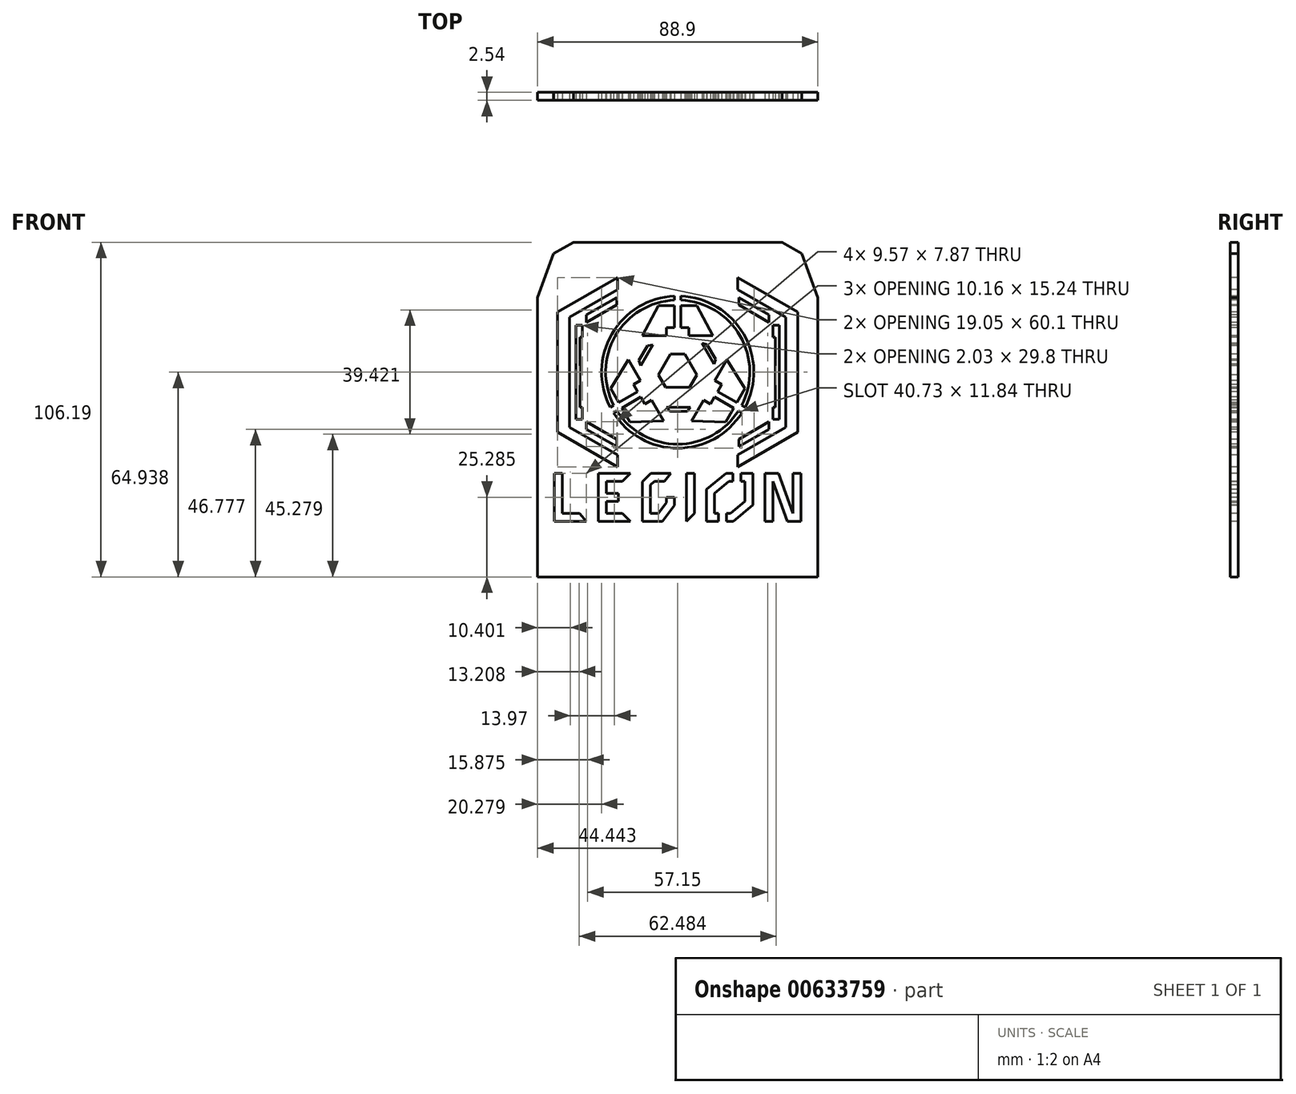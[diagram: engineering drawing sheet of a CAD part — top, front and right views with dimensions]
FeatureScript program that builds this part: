
annotation { "Feature Type Name" : "Feature", "Feature Type Description" : "" }
export const myFeature = defineFeature(function(context is Context, id is Id, definition is map)
    precondition{}
    {
        {
            var Q0;
            Q0=qCreatedBy(makeId("Front.planeOp"),FACE);
            var sketch = newSketch(context, id + "F0", { "sketchPlane" : qUnion([Q0])});
            skLineSegment(sketch, "E0.0", {"start": v(-38.1, -19.1) * mm, "end": v(-38.1, 19) * mm});
            skLineSegment(sketch, "E0.1", {"start": v(-38.1, 19) * mm, "end": v(-19.05, 30) * mm});
            skLineSegment(sketch, "E0.2", {"start": v(19.05, 30) * mm, "end": v(38.1, 19) * mm});
            skLineSegment(sketch, "E0.3", {"start": v(38.1, 19) * mm, "end": v(38.1, -19.1) * mm});
            skLineSegment(sketch, "E0.4", {"start": v(38.1, -19.1) * mm, "end": v(19.05, -30.1) * mm});
            skLineSegment(sketch, "E0.5", {"start": v(-19.05, -30.1) * mm, "end": v(-38.1, -19.1) * mm});
            skLineSegment(sketch, "E1", {"start": v(-19.05, -30.1) * mm, "end": v(-19.05, -26.3) * mm});
            skLineSegment(sketch, "E2", {"start": v(19.05, 30) * mm, "end": v(19.05, 26.19) * mm});
            skPoint(sketch, "E3.orphan", {"position": v(0, 41) * mm});
            skPoint(sketch, "E4.orphan", {"position": v(0, -41.1) * mm});
            skLineSegment(sketch, "E5", {"start": v(19.05, -26.3) * mm, "end": v(34.29, -17.5) * mm});
            skLineSegment(sketch, "E6", {"start": v(34.29, -17.5) * mm, "end": v(34.29, 17.39) * mm});
            skLineSegment(sketch, "E7", {"start": v(34.29, 17.39) * mm, "end": v(19.05, 26.19) * mm});
            skLineSegment(sketch, "E8.trimOffspring", {"start": v(19.05, -26.3) * mm, "end": v(19.05, -30.1) * mm});
            skLineSegment(sketch, "E9", {"start": v(-19.05, 26.19) * mm, "end": v(-34.3, 17.39) * mm});
            skLineSegment(sketch, "E10", {"start": v(-34.29, 17.39) * mm, "end": v(-34.29, -17.5) * mm});
            skLineSegment(sketch, "E11", {"start": v(-34.29, -17.5) * mm, "end": v(-19.05, -26.3) * mm});
            skLineSegment(sketch, "E12.trimOffspring", {"start": v(-19.05, 26.19) * mm, "end": v(-19.05, 30) * mm});
            skSolve(sketch);
        }
        {
            var Q0;
            Q0=makeQuery(id+"F0.imprint","IMPRINT",FACE,{"disambiguationData":[TD([[makeQuery(id+"F0.imprint","IMPRINT",EDGE,{"derivedFrom":sQuery(id+"F0.wireOp",EDGE,"E0.0")}),-1.0]])]});
            var sketch = newSketch(context, id + "F1", { "sketchPlane" : qUnion([Q0])});
            skLineSegment(sketch, "E13", {"start": v(-1.02, 14.1) * mm, "end": v(-3.56, 14.1) * mm});
            skLineSegment(sketch, "E14", {"start": v(-3.56, 14.1) * mm, "end": v(-3.56, 11.56) * mm});
            skLineSegment(sketch, "E15", {"start": v(-3.56, 11.56) * mm, "end": v(-11.18, 11.56) * mm});
            skLineSegment(sketch, "E16", {"start": v(1.02, 14.1) * mm, "end": v(3.56, 14.1) * mm});
            skLineSegment(sketch, "E17", {"start": v(3.56, 14.1) * mm, "end": v(3.56, 11.56) * mm});
            skLineSegment(sketch, "E18", {"start": v(3.56, 11.56) * mm, "end": v(11.18, 11.56) * mm});
            skLineSegment(sketch, "E19", {"start": v(-11.18, 11.56) * mm, "end": v(-6.1, 21.08) * mm});
            skLineSegment(sketch, "E20", {"start": v(11.18, 11.56) * mm, "end": v(6.1, 21.08) * mm});
            skLineSegment(sketch, "E21", {"start": v(-6.1, 21.08) * mm, "end": v(-1.02, 21.08) * mm});
            skLineSegment(sketch, "E22", {"start": v(-1.02, 14.1) * mm, "end": v(-1.02, 21.08) * mm});
            skLineSegment(sketch, "E23", {"start": v(1.02, 14.1) * mm, "end": v(1.02, 21.08) * mm});
            skLineSegment(sketch, "E24.trimOffspring", {"start": v(1.02, 21.08) * mm, "end": v(6.1, 21.08) * mm});
            skLineSegment(sketch, "E25.1.0", {"start": v(-8.23, -8.86) * mm, "end": v(-4.42, -15.46) * mm});
            skLineSegment(sketch, "E25.1.1", {"start": v(-4.42, -15.46) * mm, "end": v(-15.2, -15.82) * mm});
            skLineSegment(sketch, "E25.1.2", {"start": v(-15.2, -15.82) * mm, "end": v(-17.75, -11.42) * mm});
            skLineSegment(sketch, "E25.1.3", {"start": v(-11.7, -7.93) * mm, "end": v(-17.75, -11.42) * mm});
            skLineSegment(sketch, "E25.1.4", {"start": v(-11.7, -7.93) * mm, "end": v(-10.43, -10.13) * mm});
            skLineSegment(sketch, "E25.1.5", {"start": v(-10.43, -10.13) * mm, "end": v(-8.23, -8.86) * mm});
            skLineSegment(sketch, "E25.1.6", {"start": v(-13.98, -3.97) * mm, "end": v(-11.79, -2.7) * mm});
            skLineSegment(sketch, "E25.1.7", {"start": v(-12.71, -6.17) * mm, "end": v(-13.98, -3.97) * mm});
            skLineSegment(sketch, "E25.1.8", {"start": v(-11.79, -2.7) * mm, "end": v(-15.6, 3.9) * mm});
            skLineSegment(sketch, "E25.1.9", {"start": v(-15.6, 3.9) * mm, "end": v(-21.3, -5.26) * mm});
            skLineSegment(sketch, "E25.1.10", {"start": v(-12.71, -6.17) * mm, "end": v(-18.76, -9.66) * mm});
            skLineSegment(sketch, "E25.1.11", {"start": v(-18.76, -9.66) * mm, "end": v(-21.3, -5.26) * mm});
            skLineSegment(sketch, "E25.2.0", {"start": v(11.79, -2.7) * mm, "end": v(15.6, 3.9) * mm});
            skLineSegment(sketch, "E25.2.1", {"start": v(15.6, 3.9) * mm, "end": v(21.3, -5.26) * mm});
            skLineSegment(sketch, "E25.2.2", {"start": v(21.3, -5.26) * mm, "end": v(18.76, -9.66) * mm});
            skLineSegment(sketch, "E25.2.3", {"start": v(12.71, -6.17) * mm, "end": v(18.76, -9.66) * mm});
            skLineSegment(sketch, "E25.2.4", {"start": v(12.71, -6.17) * mm, "end": v(13.98, -3.97) * mm});
            skLineSegment(sketch, "E25.2.5", {"start": v(13.98, -3.97) * mm, "end": v(11.79, -2.7) * mm});
            skLineSegment(sketch, "E25.2.6", {"start": v(10.43, -10.13) * mm, "end": v(8.23, -8.86) * mm});
            skLineSegment(sketch, "E25.2.7", {"start": v(11.7, -7.93) * mm, "end": v(10.43, -10.13) * mm});
            skLineSegment(sketch, "E25.2.8", {"start": v(8.23, -8.86) * mm, "end": v(4.42, -15.46) * mm});
            skLineSegment(sketch, "E25.2.9", {"start": v(4.42, -15.46) * mm, "end": v(15.2, -15.82) * mm});
            skLineSegment(sketch, "E25.2.10", {"start": v(11.7, -7.93) * mm, "end": v(17.75, -11.42) * mm});
            skLineSegment(sketch, "E25.2.11", {"start": v(17.75, -11.42) * mm, "end": v(15.2, -15.82) * mm});
            skPoint(sketch, "E25.center", {"position": v(0, 0) * mm});
            skLineSegment(sketch, "E26", {"start": v(-6.1, -0.88) * mm, "end": v(-2.29, 5.72) * mm});
            skLineSegment(sketch, "E27", {"start": v(-2.29, 5.72) * mm, "end": v(2.29, 5.72) * mm});
            skLineSegment(sketch, "E28", {"start": v(2.29, 5.72) * mm, "end": v(6.1, -0.88) * mm});
            skLineSegment(sketch, "E29", {"start": v(6.1, -0.88) * mm, "end": v(3.8, -4.84) * mm});
            skLineSegment(sketch, "E30", {"start": v(3.8, -4.84) * mm, "end": v(-3.81, -4.84) * mm});
            skLineSegment(sketch, "E31", {"start": v(-3.81, -4.84) * mm, "end": v(-6.1, -0.88) * mm});
            skLineSegment(sketch, "E32", {"start": v(-7.91, 8.67) * mm, "end": v(-11.72, 2.08) * mm});
            skLineSegment(sketch, "E33", {"start": v(-11.72, 2.08) * mm, "end": v(-12.29, 3.63) * mm});
            skLineSegment(sketch, "E34", {"start": v(-12.29, 3.63) * mm, "end": v(-9.54, 8.39) * mm});
            skLineSegment(sketch, "E35", {"start": v(-9.54, 8.39) * mm, "end": v(-7.91, 8.67) * mm});
            skLineSegment(sketch, "E36", {"start": v(-11.72, 2.08) * mm, "end": v(-12.86, 2.73) * mm});
            skLineSegment(sketch, "E37", {"start": v(-7.91, 8.67) * mm, "end": v(-9.11, 9.37) * mm});
            skLineSegment(sketch, "E38.1.0", {"start": v(-2.5, -12.46) * mm, "end": v(-3.56, -11.19) * mm});
            skLineSegment(sketch, "E38.1.1", {"start": v(3, -12.46) * mm, "end": v(-2.5, -12.46) * mm});
            skLineSegment(sketch, "E38.1.2", {"start": v(-3.56, -11.19) * mm, "end": v(4.06, -11.19) * mm});
            skLineSegment(sketch, "E38.1.3", {"start": v(4.06, -11.19) * mm, "end": v(3, -12.46) * mm});
            skLineSegment(sketch, "E38.2.0", {"start": v(12.04, 4.07) * mm, "end": v(11.47, 2.52) * mm});
            skLineSegment(sketch, "E38.2.1", {"start": v(9.3, 8.83) * mm, "end": v(12.04, 4.07) * mm});
            skLineSegment(sketch, "E38.2.2", {"start": v(11.47, 2.52) * mm, "end": v(7.66, 9.11) * mm});
            skLineSegment(sketch, "E38.2.3", {"start": v(7.66, 9.11) * mm, "end": v(9.3, 8.83) * mm});
            skArc(sketch, "E39", {"start": v(-1.01, 24.1) * mm, "mid": v(-20.9, 12.08) * mm, "end": v(-21.4, -11.16) * mm});
            skLineSegment(sketch, "E40", {"start": v(-1.01, 22.84) * mm, "end": v(-1.01, 24.1) * mm});
            skLineSegment(sketch, "E41", {"start": v(1.04, 22.84) * mm, "end": v(1.04, 24.1) * mm});
            skLineSegment(sketch, "E42.1.0", {"start": v(-19.27, -12.3) * mm, "end": v(-20.37, -12.93) * mm});
            skLineSegment(sketch, "E42.1.1", {"start": v(-20.3, -10.52) * mm, "end": v(-21.4, -11.16) * mm});
            skLineSegment(sketch, "E42.2.0", {"start": v(20.28, -10.54) * mm, "end": v(21.38, -11.18) * mm});
            skLineSegment(sketch, "E42.2.1", {"start": v(19.26, -12.32) * mm, "end": v(20.36, -12.95) * mm});
            skArc(sketch, "E43.trimOffspring", {"start": v(-20.37, -12.93) * mm, "mid": v(-0.01, -24.13) * mm, "end": v(20.36, -12.95) * mm});
            skArc(sketch, "E44.trimOffspring", {"start": v(21.38, -11.18) * mm, "mid": v(20.9, 12.05) * mm, "end": v(1.04, 24.1) * mm});
            skArc(sketch, "E45", {"start": v(20.28, -10.54) * mm, "mid": v(19.8, 11.42) * mm, "end": v(1.04, 22.84) * mm});
            skArc(sketch, "E46.trimOffspring", {"start": v(-19.27, -12.3) * mm, "mid": v(-0.01, -22.86) * mm, "end": v(19.26, -12.32) * mm});
            skArc(sketch, "E47.trimOffspring", {"start": v(-1.01, 22.84) * mm, "mid": v(-19.8, 11.44) * mm, "end": v(-20.3, -10.52) * mm});
            skSolve(sketch);
        }
        {
            var Q0;
            Q0=makeQuery(id+"F0.imprint","IMPRINT",FACE,{"disambiguationData":[TD([[makeQuery(id+"F0.imprint","IMPRINT",EDGE,{"derivedFrom":sQuery(id+"F0.wireOp",EDGE,"E0.0")}),-1.0]])]});
            var sketch = newSketch(context, id + "F2", { "sketchPlane" : qUnion([Q0])});
            skLineSegment(sketch, "E48.bottom", {"start": v(-44.45, -65) * mm, "end": v(44.45, -65) * mm});
            skLineSegment(sketch, "E48.top", {"start": v(-44.45, 49.3) * mm, "end": v(44.45, 49.3) * mm});
            skLineSegment(sketch, "E48.left", {"start": v(-44.45, -65) * mm, "end": v(-44.45, 49.3) * mm});
            skLineSegment(sketch, "E48.right", {"start": v(44.45, -65) * mm, "end": v(44.45, 49.3) * mm});
            skSolve(sketch);
        }
        {
            var Q0;
            Q0=makeQuery(id+"F2.imprint","IMPRINT",FACE,{"disambiguationData":[TD([[makeQuery(id+"F2.imprint","IMPRINT",EDGE,{"derivedFrom":sQuery(id+"F2.wireOp",EDGE,"E48.bottom")}),1.0]])]});
            extrude(context, id + "F3", {"entities" : qUnion([Q0]), "oppositeDirection" : true, "depth" : 2.54 * mm, "offsetDistance" : 25.4 * mm});
        }
        {
            var Q0;
            Q0=makeQuery(id+"F0.imprint","IMPRINT",FACE,{"disambiguationData":[TD([[makeQuery(id+"F0.imprint","IMPRINT",EDGE,{"derivedFrom":sQuery(id+"F0.wireOp",EDGE,"E0.2")}),-1.0]])]});
            extrude(context, id + "F4", {"entities" : qUnion([Q0]), "operationType" : NewBodyOperationType.REMOVE, "oppositeDirection" : true, "depth" : 25.4 * mm, "offsetDistance" : 25.4 * mm});
        }
        {
            var Q0;
            Q0=makeQuery(id+"F1.imprint","IMPRINT",FACE,{"disambiguationData":[TD([[makeQuery(id+"F1.imprint","IMPRINT",EDGE,{"derivedFrom":sQuery(id+"F1.wireOp",EDGE,"E25.1.6")}),1.0]])]});
            var Q1;
            Q1=makeQuery(id+"F1.imprint","IMPRINT",FACE,{"disambiguationData":[TD([[makeQuery(id+"F1.imprint","IMPRINT",EDGE,{"derivedFrom":sQuery(id+"F1.wireOp",EDGE,"E25.1.0")}),-1.0]])]});
            var Q2;
            Q2=makeQuery(id+"F1.imprint","IMPRINT",FACE,{"disambiguationData":[TD([[makeQuery(id+"F1.imprint","IMPRINT",EDGE,{"derivedFrom":sQuery(id+"F1.wireOp",EDGE,"E25.2.6")}),1.0]])]});
            var Q3;
            Q3=makeQuery(id+"F1.imprint","IMPRINT",FACE,{"disambiguationData":[TD([[makeQuery(id+"F1.imprint","IMPRINT",EDGE,{"derivedFrom":sQuery(id+"F1.wireOp",EDGE,"E38.1.0")}),-1.0]])]});
            var Q4;
            Q4=makeQuery(id+"F1.imprint","IMPRINT",FACE,{"disambiguationData":[TD([[makeQuery(id+"F1.imprint","IMPRINT",EDGE,{"derivedFrom":sQuery(id+"F1.wireOp",EDGE,"E25.2.0")}),-1.0]])]});
            var Q5;
            Q5=makeQuery(id+"F1.imprint","IMPRINT",FACE,{"disambiguationData":[TD([[makeQuery(id+"F1.imprint","IMPRINT",EDGE,{"derivedFrom":sQuery(id+"F1.wireOp",EDGE,"E38.2.0")}),-1.0]])]});
            var Q6;
            Q6=makeQuery(id+"F1.imprint","IMPRINT",FACE,{"disambiguationData":[TD([[makeQuery(id+"F1.imprint","IMPRINT",EDGE,{"derivedFrom":sQuery(id+"F1.wireOp",EDGE,"E26")}),-1.0]])]});
            var Q7;
            Q7=makeQuery(id+"F1.imprint","IMPRINT",FACE,{"disambiguationData":[TD([[makeQuery(id+"F1.imprint","IMPRINT",EDGE,{"derivedFrom":sQuery(id+"F1.wireOp",EDGE,"E32")}),-1.0]])]});
            var Q8;
            Q8=makeQuery(id+"F1.imprint","IMPRINT",FACE,{"disambiguationData":[TD([[makeQuery(id+"F1.imprint","IMPRINT",EDGE,{"derivedFrom":sQuery(id+"F1.wireOp",EDGE,"E16")}),1.0]])]});
            var Q9;
            Q9=makeQuery(id+"F1.imprint","IMPRINT",FACE,{"disambiguationData":[TD([[makeQuery(id+"F1.imprint","IMPRINT",EDGE,{"derivedFrom":sQuery(id+"F1.wireOp",EDGE,"E13")}),-1.0]])]});
            var Q10;
            Q10=makeQuery(id+"F1.imprint","IMPRINT",FACE,{"disambiguationData":[TD([[makeQuery(id+"F1.imprint","IMPRINT",EDGE,{"derivedFrom":sQuery(id+"F1.wireOp",EDGE,"E42.2.0")}),1.0]])]});
            var Q11;
            Q11=makeQuery(id+"F1.imprint","IMPRINT",FACE,{"disambiguationData":[TD([[makeQuery(id+"F1.imprint","IMPRINT",EDGE,{"derivedFrom":sQuery(id+"F1.wireOp",EDGE,"E42.1.0")}),1.0]])]});
            var Q12;
            {var subQ0=sQuery(id+"F1.wireOp",EDGE,"E39");Q12=makeQuery(id+"F1.imprint","IMPRINT",FACE,{"disambiguationData":[TD([[makeQuery(id+"F1.imprint","IMPRINT",EDGE,{"derivedFrom":subQ0}),1.0]])]});}
            extrude(context, id + "F5", {"entities" : qUnion([Q0, Q1, Q2, Q3, Q4, Q5, Q6, Q7, Q8, Q9, Q10, Q11, Q12]), "operationType" : NewBodyOperationType.REMOVE, "oppositeDirection" : true, "depth" : 25.4 * mm, "offsetDistance" : 25.4 * mm});
        }
        {
            var Q0;
            Q0=makeQuery(id+"F3.opExtrude","CAP_FACE",FACE,{"disambiguationData":[OSD([sQuery(id+"F0.wireOp",EDGE,"E0.0"),sQuery(id+"F0.wireOp",EDGE,"E0.1"),sQuery(id+"F0.wireOp",EDGE,"E0.5"),sQuery(id+"F0.wireOp",EDGE,"E1"),sQuery(id+"F0.wireOp",EDGE,"E9"),sQuery(id+"F0.wireOp",EDGE,"E10"),sQuery(id+"F0.wireOp",EDGE,"E11"),sQuery(id+"F0.wireOp",EDGE,"E12.trimOffspring"),sQuery(id+"F2.wireOp",EDGE,"E48.bottom"),sQuery(id+"F2.wireOp",EDGE,"E48.top"),sQuery(id+"F2.wireOp",EDGE,"E48.left"),sQuery(id+"F2.wireOp",EDGE,"E48.right")])],"isStart":true});
            var sketch = newSketch(context, id + "F6", { "sketchPlane" : qUnion([Q0])});
            skLineSegment(sketch, "E49", {"start": v(-39.13, -32.08) * mm, "end": v(-39.13, -47.32) * mm});
            skLineSegment(sketch, "E50", {"start": v(-39.13, -47.32) * mm, "end": v(-28.97, -47.32) * mm});
            skLineSegment(sketch, "E51", {"start": v(-28.97, -47.32) * mm, "end": v(-31.1, -44.78) * mm});
            skLineSegment(sketch, "E52", {"start": v(-31.1, -44.78) * mm, "end": v(-36.59, -44.78) * mm});
            skLineSegment(sketch, "E53", {"start": v(-36.59, -44.78) * mm, "end": v(-36.59, -32.08) * mm});
            skLineSegment(sketch, "E54", {"start": v(-36.59, -32.08) * mm, "end": v(-39.13, -32.08) * mm});
            skLineSegment(sketch, "E55", {"start": v(-25.16, -47.32) * mm, "end": v(-25.16, -32.08) * mm});
            skLineSegment(sketch, "E56", {"start": v(-25.16, -32.08) * mm, "end": v(-15, -32.08) * mm});
            skLineSegment(sketch, "E57", {"start": v(-15, -32.08) * mm, "end": v(-17.54, -34.62) * mm});
            skLineSegment(sketch, "E58", {"start": v(-17.54, -34.62) * mm, "end": v(-22.62, -34.62) * mm});
            skLineSegment(sketch, "E59", {"start": v(-22.62, -34.62) * mm, "end": v(-22.62, -38.43) * mm});
            skLineSegment(sketch, "E60", {"start": v(-22.62, -38.43) * mm, "end": v(-18.8, -38.43) * mm});
            skLineSegment(sketch, "E61", {"start": v(-18.8, -38.43) * mm, "end": v(-18.8, -40.97) * mm});
            skLineSegment(sketch, "E62", {"start": v(-18.8, -40.97) * mm, "end": v(-22.62, -40.97) * mm});
            skLineSegment(sketch, "E63", {"start": v(-22.62, -40.97) * mm, "end": v(-22.62, -44.78) * mm});
            skLineSegment(sketch, "E64", {"start": v(-22.62, -44.78) * mm, "end": v(-17.54, -44.78) * mm});
            skLineSegment(sketch, "E65", {"start": v(-17.54, -44.78) * mm, "end": v(-15, -47.32) * mm});
            skLineSegment(sketch, "E66", {"start": v(-15, -47.32) * mm, "end": v(-25.16, -47.32) * mm});
            skLineSegment(sketch, "E67", {"start": v(-2.14, -32.08) * mm, "end": v(-8.5, -32.08) * mm});
            skLineSegment(sketch, "E68", {"start": v(-8.5, -32.08) * mm, "end": v(-11.19, -34.78) * mm});
            skLineSegment(sketch, "E69", {"start": v(-11.19, -34.78) * mm, "end": v(-11.19, -47.32) * mm});
            skLineSegment(sketch, "E70", {"start": v(-11.19, -47.32) * mm, "end": v(-4.84, -47.32) * mm});
            skLineSegment(sketch, "E71", {"start": v(-4.84, -47.32) * mm, "end": v(-1.03, -42.24) * mm});
            skLineSegment(sketch, "E72", {"start": v(-1.03, -42.24) * mm, "end": v(-1.03, -39.7) * mm});
            skLineSegment(sketch, "E73", {"start": v(-1.03, -39.7) * mm, "end": v(-3.57, -39.7) * mm});
            skLineSegment(sketch, "E74", {"start": v(-3.57, -39.7) * mm, "end": v(-3.57, -41.4) * mm});
            skLineSegment(sketch, "E75", {"start": v(-3.57, -41.4) * mm, "end": v(-6.1, -44.78) * mm});
            skLineSegment(sketch, "E76", {"start": v(-6.1, -44.78) * mm, "end": v(-8.65, -44.78) * mm});
            skLineSegment(sketch, "E77", {"start": v(-8.65, -44.78) * mm, "end": v(-8.65, -35.83) * mm});
            skLineSegment(sketch, "E78", {"start": v(-8.65, -35.83) * mm, "end": v(-7.44, -34.62) * mm});
            skLineSegment(sketch, "E79", {"start": v(-2.14, -32.08) * mm, "end": v(-4.27, -34.62) * mm});
            skLineSegment(sketch, "E80", {"start": v(-4.27, -34.62) * mm, "end": v(-7.44, -34.62) * mm});
            skLineSegment(sketch, "E81", {"start": v(2.78, -32.08) * mm, "end": v(5.32, -32.08) * mm});
            skLineSegment(sketch, "E82", {"start": v(5.32, -32.08) * mm, "end": v(5.32, -44.78) * mm});
            skLineSegment(sketch, "E83", {"start": v(5.32, -44.78) * mm, "end": v(2.78, -47.32) * mm});
            skLineSegment(sketch, "E84", {"start": v(2.78, -47.32) * mm, "end": v(2.78, -32.08) * mm});
            skLineSegment(sketch, "E85", {"start": v(9.13, -47.32) * mm, "end": v(9.13, -37.25) * mm});
            skLineSegment(sketch, "E86", {"start": v(9.13, -37.25) * mm, "end": v(15.29, -32.08) * mm});
            skLineSegment(sketch, "E87", {"start": v(15.29, -32.08) * mm, "end": v(17.48, -32.08) * mm});
            skLineSegment(sketch, "E88", {"start": v(23.83, -32.08) * mm, "end": v(23.83, -42.16) * mm});
            skLineSegment(sketch, "E89", {"start": v(23.83, -42.16) * mm, "end": v(17.68, -47.32) * mm});
            skLineSegment(sketch, "E90", {"start": v(17.68, -47.32) * mm, "end": v(15.48, -47.32) * mm});
            skLineSegment(sketch, "E91", {"start": v(11.67, -44.78) * mm, "end": v(11.67, -38.43) * mm});
            skLineSegment(sketch, "E92", {"start": v(11.67, -38.43) * mm, "end": v(16.21, -34.62) * mm});
            skLineSegment(sketch, "E93", {"start": v(16.21, -34.62) * mm, "end": v(17.48, -34.62) * mm});
            skLineSegment(sketch, "E94", {"start": v(21.3, -34.62) * mm, "end": v(21.3, -40.97) * mm});
            skLineSegment(sketch, "E95", {"start": v(21.3, -40.97) * mm, "end": v(16.75, -44.78) * mm});
            skLineSegment(sketch, "E96", {"start": v(16.75, -44.78) * mm, "end": v(15.48, -44.78) * mm});
            skLineSegment(sketch, "E97", {"start": v(27.64, -47.32) * mm, "end": v(27.64, -32.08) * mm});
            skLineSegment(sketch, "E98", {"start": v(27.64, -32.08) * mm, "end": v(31.96, -32.08) * mm});
            skLineSegment(sketch, "E99", {"start": v(31.96, -32.08) * mm, "end": v(36.58, -44.78) * mm});
            skLineSegment(sketch, "E100", {"start": v(36.58, -44.78) * mm, "end": v(36.58, -32.08) * mm});
            skLineSegment(sketch, "E101", {"start": v(36.58, -32.08) * mm, "end": v(39.12, -32.08) * mm});
            skLineSegment(sketch, "E102", {"start": v(39.12, -32.08) * mm, "end": v(39.12, -47.32) * mm});
            skLineSegment(sketch, "E103", {"start": v(39.12, -47.32) * mm, "end": v(34.8, -47.32) * mm});
            skLineSegment(sketch, "E104", {"start": v(34.8, -47.32) * mm, "end": v(30.18, -34.62) * mm});
            skLineSegment(sketch, "E105", {"start": v(30.18, -34.62) * mm, "end": v(30.18, -47.32) * mm});
            skLineSegment(sketch, "E106", {"start": v(30.18, -47.32) * mm, "end": v(27.64, -47.32) * mm});
            skLineSegment(sketch, "E107", {"start": v(17.48, -34.62) * mm, "end": v(17.48, -32.08) * mm});
            skLineSegment(sketch, "E108", {"start": v(20.02, -34.62) * mm, "end": v(20.02, -32.08) * mm});
            skLineSegment(sketch, "E109", {"start": v(12.94, -44.78) * mm, "end": v(12.94, -47.32) * mm});
            skLineSegment(sketch, "E110", {"start": v(15.48, -44.78) * mm, "end": v(15.48, -47.32) * mm});
            skLineSegment(sketch, "E111.trimOffspring", {"start": v(20.02, -34.62) * mm, "end": v(21.3, -34.62) * mm});
            skLineSegment(sketch, "E112.trimOffspring", {"start": v(20.02, -32.08) * mm, "end": v(23.83, -32.08) * mm});
            skLineSegment(sketch, "E113.trimOffspring", {"start": v(12.94, -44.78) * mm, "end": v(11.67, -44.78) * mm});
            skLineSegment(sketch, "E114.trimOffspring", {"start": v(12.94, -47.32) * mm, "end": v(9.13, -47.32) * mm});
            skSolve(sketch);
        }
        {
            var Q0;
            Q0=makeQuery(id+"F6.imprint","IMPRINT",FACE,{"disambiguationData":[TD([[makeQuery(id+"F6.imprint","IMPRINT",EDGE,{"derivedFrom":sQuery(id+"F6.wireOp",EDGE,"E49")}),1.0]])]});
            var Q1;
            Q1=makeQuery(id+"F6.imprint","IMPRINT",FACE,{"disambiguationData":[TD([[makeQuery(id+"F6.imprint","IMPRINT",EDGE,{"derivedFrom":sQuery(id+"F6.wireOp",EDGE,"E55")}),-1.0]])]});
            var Q2;
            Q2=makeQuery(id+"F6.imprint","IMPRINT",FACE,{"disambiguationData":[TD([[makeQuery(id+"F6.imprint","IMPRINT",EDGE,{"derivedFrom":sQuery(id+"F6.wireOp",EDGE,"E67")}),1.0]])]});
            var Q3;
            Q3=makeQuery(id+"F6.imprint","IMPRINT",FACE,{"disambiguationData":[TD([[makeQuery(id+"F6.imprint","IMPRINT",EDGE,{"derivedFrom":sQuery(id+"F6.wireOp",EDGE,"E81")}),-1.0]])]});
            var Q4;
            Q4=makeQuery(id+"F6.imprint","IMPRINT",FACE,{"disambiguationData":[TD([[makeQuery(id+"F6.imprint","IMPRINT",EDGE,{"derivedFrom":sQuery(id+"F6.wireOp",EDGE,"E85")}),-1.0]])]});
            var Q5;
            Q5=makeQuery(id+"F6.imprint","IMPRINT",FACE,{"disambiguationData":[TD([[makeQuery(id+"F6.imprint","IMPRINT",EDGE,{"derivedFrom":sQuery(id+"F6.wireOp",EDGE,"E97")}),-1.0]])]});
            var Q6;
            Q6=makeQuery(id+"F6.imprint","IMPRINT",FACE,{"disambiguationData":[TD([[makeQuery(id+"F6.imprint","IMPRINT",EDGE,{"derivedFrom":sQuery(id+"F6.wireOp",EDGE,"E88")}),-1.0]])]});
            extrude(context, id + "F7", {"entities" : qUnion([Q0, Q1, Q2, Q3, Q4, Q5, Q6]), "operationType" : NewBodyOperationType.REMOVE, "oppositeDirection" : true, "depth" : 25.4 * mm, "offsetDistance" : 25.4 * mm});
        }
        {
            var Q0;
            {var subQ0=sQuery(id+"F0.wireOp",EDGE,"E0.1");var subQ1=sQuery(id+"F0.wireOp",EDGE,"E9");var subQ2=sQuery(id+"F0.wireOp",EDGE,"E1");var subQ3=sQuery(id+"F0.wireOp",EDGE,"E0.0");var subQ4=sQuery(id+"F2.wireOp",EDGE,"E48.right");var subQ5=sQuery(id+"F2.wireOp",EDGE,"E48.left");var subQ6=sQuery(id+"F2.wireOp",EDGE,"E48.top");var subQ7=sQuery(id+"F0.wireOp",EDGE,"E12.trimOffspring");var subQ8=sQuery(id+"F0.wireOp",EDGE,"E11");var subQ9=sQuery(id+"F0.wireOp",EDGE,"E0.5");var subQ10=sQuery(id+"F2.wireOp",EDGE,"E48.bottom");var subQ11=sQuery(id+"F0.wireOp",EDGE,"E10");Q0=makeQuery(id+"F7.boolean.opBoolean","SPLIT",FACE,{"disambiguationData":[TD([makeQuery(id+"F3.opExtrude","SWEPT_FACE",FACE,{"disambiguationData":[OSD([subQ10])]})])],"derivedFrom":makeQuery(id+"F3.opExtrude","CAP_FACE",FACE,{"disambiguationData":[OSD([subQ3,subQ0,subQ9,subQ2,subQ1,subQ11,subQ8,subQ7,subQ10,subQ6,subQ5,subQ4])],"isStart":true})});}
            var sketch = newSketch(context, id + "F8", { "sketchPlane" : qUnion([Q0])});
            skLineSegment(sketch, "E115", {"start": v(-44.45, 34.64) * mm, "end": v(-19.05, 49.3) * mm});
            skLineSegment(sketch, "E116", {"start": v(19.05, 49.3) * mm, "end": v(44.45, 34.64) * mm});
            skLineSegment(sketch, "E117", {"start": v(-39.37, 37.58) * mm, "end": v(-44.45, 23.62) * mm});
            skLineSegment(sketch, "E118", {"start": v(39.37, 37.58) * mm, "end": v(44.45, 23.62) * mm});
            skLineSegment(sketch, "E119", {"start": v(-33.1, 41.2) * mm, "end": v(33.1, 41.2) * mm});
            skSolve(sketch);
        }
        {
            var Q0;
            {var subQ0=sQuery(id+"F8.wireOp",EDGE,"E115");Q0=makeQuery(id+"F8.imprint","IMPRINT",FACE,{"disambiguationData":[TD([[makeQuery(id+"F8.imprint","IMPRINT",EDGE,{"derivedFrom":subQ0}),1.0]])]});}
            var Q1;
            {var subQ0=sQuery(id+"F8.wireOp",EDGE,"E116");Q1=makeQuery(id+"F8.imprint","IMPRINT",FACE,{"disambiguationData":[TD([[makeQuery(id+"F8.imprint","IMPRINT",EDGE,{"derivedFrom":subQ0}),1.0]])]});}
            var Q2;
            {var subQ3=sQuery(id+"F8.wireOp",EDGE,"E117");Q2=makeQuery(id+"F8.imprint","IMPRINT",FACE,{"disambiguationData":[TD([[makeQuery(id+"F8.imprint","IMPRINT",EDGE,{"derivedFrom":subQ3}),-1.0]])]});}
            var Q3;
            {var subQ3=sQuery(id+"F8.wireOp",EDGE,"E118");Q3=makeQuery(id+"F8.imprint","IMPRINT",FACE,{"disambiguationData":[TD([[makeQuery(id+"F8.imprint","IMPRINT",EDGE,{"derivedFrom":subQ3}),1.0]])]});}
            var Q4;
            {var subQ3=sQuery(id+"F8.wireOp",EDGE,"E119");Q4=makeQuery(id+"F8.imprint","IMPRINT",FACE,{"disambiguationData":[TD([[makeQuery(id+"F8.imprint","IMPRINT",EDGE,{"derivedFrom":subQ3}),1.0]])]});}
            extrude(context, id + "F9", {"entities" : qUnion([Q0, Q1, Q2, Q3, Q4]), "operationType" : NewBodyOperationType.REMOVE, "oppositeDirection" : true, "depth" : 25.4 * mm, "offsetDistance" : 25.4 * mm});
        }
        {
            var Q0;
            Q0=makeQuery(id+"F3.opExtrude","CAP_FACE",FACE,{"disambiguationData":[OSD([sQuery(id+"F0.wireOp",EDGE,"E0.0"),sQuery(id+"F0.wireOp",EDGE,"E0.1"),sQuery(id+"F0.wireOp",EDGE,"E0.5"),sQuery(id+"F0.wireOp",EDGE,"E1"),sQuery(id+"F0.wireOp",EDGE,"E9"),sQuery(id+"F0.wireOp",EDGE,"E10"),sQuery(id+"F0.wireOp",EDGE,"E11"),sQuery(id+"F0.wireOp",EDGE,"E12.trimOffspring"),sQuery(id+"F2.wireOp",EDGE,"E48.bottom"),sQuery(id+"F2.wireOp",EDGE,"E48.top"),sQuery(id+"F2.wireOp",EDGE,"E48.left"),sQuery(id+"F2.wireOp",EDGE,"E48.right")])],"isStart":true});
            var sketch = newSketch(context, id + "F10", { "sketchPlane" : qUnion([Q0])});
            skLineSegment(sketch, "E120", {"start": v(-32.26, -14.95) * mm, "end": v(-32.26, 14.85) * mm});
            skLineSegment(sketch, "E121", {"start": v(-32.26, 14.85) * mm, "end": v(-30.23, 14.85) * mm});
            skLineSegment(sketch, "E122", {"start": v(-30.23, -14.95) * mm, "end": v(-32.26, -14.95) * mm});
            skLineSegment(sketch, "E123", {"start": v(-30.23, 14.85) * mm, "end": v(-30.23, 11.04) * mm});
            skLineSegment(sketch, "E124", {"start": v(-30.23, 11.04) * mm, "end": v(-30.99, 11.04) * mm});
            skLineSegment(sketch, "E125", {"start": v(-30.99, 11.04) * mm, "end": v(-30.99, -11.14) * mm});
            skLineSegment(sketch, "E126", {"start": v(-30.99, -11.14) * mm, "end": v(-30.23, -11.14) * mm});
            skLineSegment(sketch, "E127", {"start": v(-30.23, -11.14) * mm, "end": v(-30.23, -14.95) * mm});
            skLineSegment(sketch, "E128", {"start": v(0, 0) * mm, "end": v(0, 29.66) * mm});
            skLineSegment(sketch, "E129.MirrorCS", {"start": v(-29.72, -14.95) * mm, "end": v(-29.72, 14.85) * mm});
            skLineSegment(sketch, "E130.MirrorCS", {"start": v(30.99, 11.04) * mm, "end": v(30.99, -11.14) * mm});
            skLineSegment(sketch, "E131.MirrorCS", {"start": v(30.23, 11.04) * mm, "end": v(30.99, 11.04) * mm});
            skLineSegment(sketch, "E132.MirrorCS", {"start": v(30.23, -14.95) * mm, "end": v(32.26, -14.95) * mm});
            skLineSegment(sketch, "E133.MirrorCS", {"start": v(32.26, -14.95) * mm, "end": v(32.26, 14.85) * mm});
            skLineSegment(sketch, "E134.MirrorCS", {"start": v(32.26, 14.85) * mm, "end": v(30.23, 14.85) * mm});
            skLineSegment(sketch, "E135.MirrorCS", {"start": v(30.99, -11.14) * mm, "end": v(30.23, -11.14) * mm});
            skLineSegment(sketch, "E136", {"start": v(30.23, -14.95) * mm, "end": v(30.23, -11.14) * mm});
            skLineSegment(sketch, "E137", {"start": v(30.23, 11.04) * mm, "end": v(30.23, 14.85) * mm});
            skSolve(sketch);
        }
        {
            var Q0;
            Q0=makeQuery(id+"F10.imprint","IMPRINT",FACE,{"disambiguationData":[TD([[makeQuery(id+"F10.imprint","IMPRINT",EDGE,{"derivedFrom":sQuery(id+"F10.wireOp",EDGE,"E120")}),-1.0]])]});
            var Q1;
            Q1=makeQuery(id+"F10.imprint","IMPRINT",FACE,{"disambiguationData":[TD([[makeQuery(id+"F10.imprint","IMPRINT",EDGE,{"derivedFrom":sQuery(id+"F10.wireOp",EDGE,"E130.MirrorCS")}),1.0]])]});
            extrude(context, id + "F11", {"entities" : qUnion([Q0, Q1]), "operationType" : NewBodyOperationType.REMOVE, "oppositeDirection" : true, "depth" : 25.4 * mm, "offsetDistance" : 25.4 * mm});
        }
        {
            var Q0;
            Q0=makeQuery(id+"F3.opExtrude","CAP_FACE",FACE,{"disambiguationData":[OSD([sQuery(id+"F0.wireOp",EDGE,"E0.0"),sQuery(id+"F0.wireOp",EDGE,"E0.1"),sQuery(id+"F0.wireOp",EDGE,"E0.5"),sQuery(id+"F0.wireOp",EDGE,"E1"),sQuery(id+"F0.wireOp",EDGE,"E9"),sQuery(id+"F0.wireOp",EDGE,"E10"),sQuery(id+"F0.wireOp",EDGE,"E11"),sQuery(id+"F0.wireOp",EDGE,"E12.trimOffspring"),sQuery(id+"F2.wireOp",EDGE,"E48.bottom"),sQuery(id+"F2.wireOp",EDGE,"E48.top"),sQuery(id+"F2.wireOp",EDGE,"E48.left"),sQuery(id+"F2.wireOp",EDGE,"E48.right")])],"isStart":true});
            var sketch = newSketch(context, id + "F12", { "sketchPlane" : qUnion([Q0])});
            skLineSegment(sketch, "E138", {"start": v(-28.96, 18.12) * mm, "end": v(-28.96, 15.77) * mm});
            skLineSegment(sketch, "E139", {"start": v(-28.96, 15.77) * mm, "end": v(-19.39, 21.3) * mm});
            skLineSegment(sketch, "E140", {"start": v(-19.39, 21.3) * mm, "end": v(-19.39, 23.65) * mm});
            skLineSegment(sketch, "E141", {"start": v(-19.39, 23.65) * mm, "end": v(-28.96, 18.12) * mm});
            skLineSegment(sketch, "E142", {"start": v(0, 0) * mm, "end": v(-20.1, 0) * mm});
            skLineSegment(sketch, "E143", {"start": v(0, 0) * mm, "end": v(0, 16) * mm});
            skLineSegment(sketch, "E144.MirrorCS", {"start": v(28.96, 15.77) * mm, "end": v(19.39, 21.3) * mm});
            skLineSegment(sketch, "E145.MirrorCS", {"start": v(19.39, 23.65) * mm, "end": v(28.96, 18.12) * mm});
            skLineSegment(sketch, "E146.MirrorCS", {"start": v(28.96, 18.12) * mm, "end": v(28.96, 15.77) * mm});
            skLineSegment(sketch, "E147.MirrorCS", {"start": v(19.39, 21.3) * mm, "end": v(19.39, 23.65) * mm});
            skLineSegment(sketch, "E148.MirrorCS", {"start": v(-28.96, -15.77) * mm, "end": v(-19.39, -21.3) * mm});
            skLineSegment(sketch, "E149.MirrorCS", {"start": v(-19.39, -23.65) * mm, "end": v(-28.96, -18.12) * mm});
            skLineSegment(sketch, "E150.MirrorCS", {"start": v(-28.96, -18.12) * mm, "end": v(-28.96, -15.77) * mm});
            skLineSegment(sketch, "E151.MirrorCS", {"start": v(-19.39, -21.3) * mm, "end": v(-19.39, -23.65) * mm});
            skLineSegment(sketch, "E152.MirrorCS", {"start": v(28.96, -15.77) * mm, "end": v(19.39, -21.3) * mm});
            skLineSegment(sketch, "E153.MirrorCS", {"start": v(19.39, -23.65) * mm, "end": v(28.96, -18.12) * mm});
            skLineSegment(sketch, "E154.MirrorCS", {"start": v(28.96, -18.12) * mm, "end": v(28.96, -15.77) * mm});
            skLineSegment(sketch, "E155.MirrorCS", {"start": v(19.39, -21.3) * mm, "end": v(19.39, -23.65) * mm});
            skSolve(sketch);
        }
        {
            var Q0;
            Q0=makeQuery(id+"F12.imprint","IMPRINT",FACE,{"disambiguationData":[TD([[makeQuery(id+"F12.imprint","IMPRINT",EDGE,{"derivedFrom":sQuery(id+"F12.wireOp",EDGE,"E138")}),1.0]])]});
            var Q1;
            Q1=makeQuery(id+"F12.imprint","IMPRINT",FACE,{"disambiguationData":[TD([[makeQuery(id+"F12.imprint","IMPRINT",EDGE,{"derivedFrom":sQuery(id+"F12.wireOp",EDGE,"E148.MirrorCS")}),-1.0]])]});
            var Q2;
            Q2=makeQuery(id+"F12.imprint","IMPRINT",FACE,{"disambiguationData":[TD([[makeQuery(id+"F12.imprint","IMPRINT",EDGE,{"derivedFrom":sQuery(id+"F12.wireOp",EDGE,"E152.MirrorCS")}),1.0]])]});
            var Q3;
            Q3=makeQuery(id+"F12.imprint","IMPRINT",FACE,{"disambiguationData":[TD([[makeQuery(id+"F12.imprint","IMPRINT",EDGE,{"derivedFrom":sQuery(id+"F12.wireOp",EDGE,"E144.MirrorCS")}),-1.0]])]});
            extrude(context, id + "F13", {"entities" : qUnion([Q0, Q1, Q2, Q3]), "operationType" : NewBodyOperationType.REMOVE, "oppositeDirection" : true, "depth" : 25.4 * mm, "offsetDistance" : 25.4 * mm});
        }
    });
